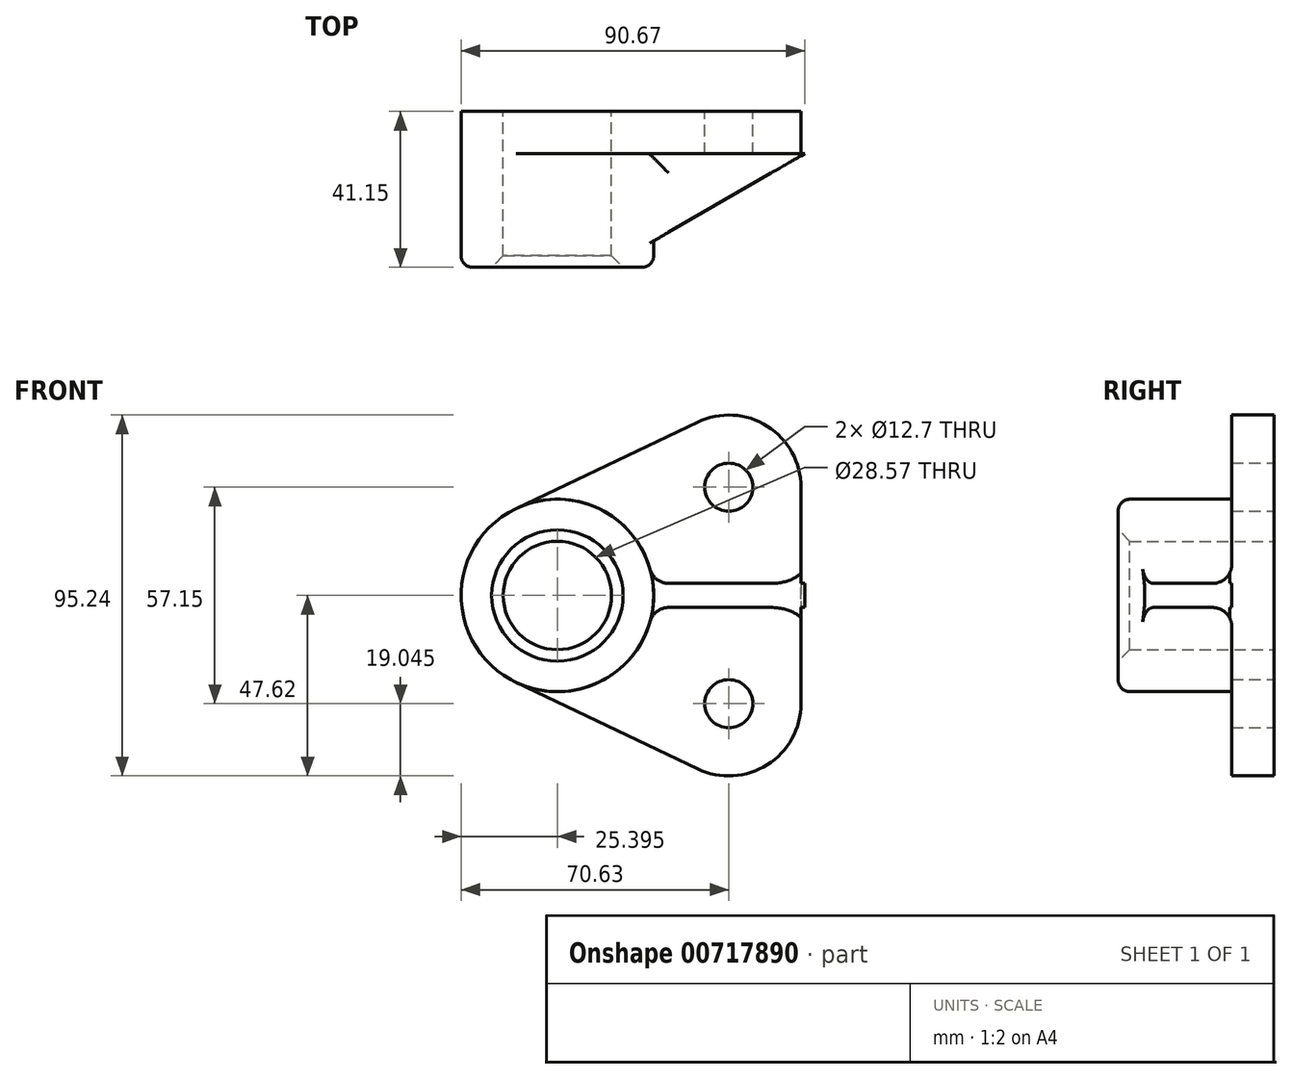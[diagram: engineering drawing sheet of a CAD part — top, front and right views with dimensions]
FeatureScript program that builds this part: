
annotation { "Feature Type Name" : "Feature", "Feature Type Description" : "" }
export const myFeature = defineFeature(function(context is Context, id is Id, definition is map)
    precondition{}
    {
        {
            var Q0;
            Q0=qCreatedBy(makeId("Front.planeOp"),FACE);
            var sketch = newSketch(context, id + "F0", { "sketchPlane" : qUnion([Q0])});
            skCircle(sketch, "E0", {"center": v(-45.23, 0) * mm, "radius": 25.4 * mm});
            skCircle(sketch, "E1", {"center": v(-45.23, 0) * mm, "radius": 14.29 * mm});
            skArc(sketch, "E2", {"start": v(19.05, 28.58) * mm, "mid": v(10.17, 44.68) * mm, "end": v(-8.2, 45.77) * mm});
            skLineSegment(sketch, "E3", {"start": v(-56.16, 22.93) * mm, "end": v(-8.2, 45.77) * mm});
            skLineSegment(sketch, "E4", {"start": v(19.05, 28.58) * mm, "end": v(19.05, -26.35) * mm});
            skLineSegment(sketch, "E5", {"start": v(-115.36, 0) * mm, "end": v(38.05, 0) * mm, "construction": true});
            skLineSegment(sketch, "E6.MirrorCS", {"start": v(-56.16, -22.93) * mm, "end": v(-8.2, -45.77) * mm});
            skArc(sketch, "E7.MirrorCS", {"start": v(19.05, -28.58) * mm, "mid": v(10.17, -44.68) * mm, "end": v(-8.2, -45.77) * mm});
            skLineSegment(sketch, "E8.MirrorCS", {"start": v(19.05, -28.58) * mm, "end": v(19.05, 26.35) * mm});
            skPoint(sketch, "E9.center.orphan", {"position": v(0, -26.35) * mm});
            skCircle(sketch, "E10", {"center": v(0, 28.58) * mm, "radius": 6.35 * mm});
            skCircle(sketch, "E11.MirrorC", {"center": v(0, -28.58) * mm, "radius": 6.35 * mm});
            skLineSegment(sketch, "E12", {"start": v(0, 28.58) * mm, "end": v(56.35, 28.58) * mm, "construction": true});
            skLineSegment(sketch, "E13", {"start": v(0, -28.58) * mm, "end": v(53.4, -28.58) * mm, "construction": true});
            skSolve(sketch);
        }
        {
            var Q0;
            Q0=makeQuery(id+"F0.imprint","IMPRINT",FACE,{"disambiguationData":[TD([[makeQuery(id+"F0.imprint","IMPRINT",EDGE,{"derivedFrom":sQuery(id+"F0.wireOp",EDGE,"E1")}),-1.0]])]});
            extrude(context, id + "F1", {"entities" : qUnion([Q0]), "depth" : 41.15 * mm, "offsetDistance" : 25.4 * mm});
        }
        {
            var Q0;
            Q0=makeQuery(id+"F1.opExtrude","CAP_EDGE",EDGE,{"disambiguationData":[OSD([sQuery(id+"F0.wireOp",EDGE,"E0")])],"isStart":false});
            fillet(context, id + "F2", {"entities" : qUnion([Q0]), "radius" : 3.05 * mm, "tangentPropagation" : true, "allowEdgeOverflow" : false});
        }
        {
            var Q0;
            Q0=makeQuery(id+"F1.opExtrude","CAP_EDGE",EDGE,{"disambiguationData":[OSD([sQuery(id+"F0.wireOp",EDGE,"E1")])],"isStart":false});
            chamfer(context, id + "F3", {"entities" : qUnion([Q0]), "width" : 3.05 * mm, "tangentPropagation" : true});
        }
        {
            var Q0;
            Q0=makeQuery(id+"F0.imprint","IMPRINT",FACE,{"disambiguationData":[TD([[makeQuery(id+"F0.imprint","IMPRINT",EDGE,{"derivedFrom":sQuery(id+"F0.wireOp",EDGE,"E2")}),1.0]])]});
            extrude(context, id + "F4", {"entities" : qUnion([Q0]), "operationType" : NewBodyOperationType.ADD, "depth" : 11.18 * mm, "offsetDistance" : 25.4 * mm});
        }
        {
            var Q0;
            Q0=qCreatedBy(makeId("Top.planeOp"),FACE);
            var sketch = newSketch(context, id + "F5", { "sketchPlane" : qUnion([Q0])});
            skLineSegment(sketch, "E14", {"start": v(-20.38, -11.14) * mm, "end": v(20.04, -11.14) * mm});
            skLineSegment(sketch, "E15", {"start": v(20.04, -11.14) * mm, "end": v(-20.38, -34.48) * mm});
            skLineSegment(sketch, "E16", {"start": v(-20.38, -34.48) * mm, "end": v(-20.38, -11.14) * mm});
            skSolve(sketch);
        }
        {
            var Q0;
            Q0=makeQuery(id+"F5.imprint","IMPRINT",FACE,{"disambiguationData":[TD([[makeQuery(id+"F5.imprint","IMPRINT",EDGE,{"derivedFrom":sQuery(id+"F5.wireOp",EDGE,"E14")}),-1.0]])]});
            var sketch = newSketch(context, id + "F6", { "sketchPlane" : qUnion([Q0])});
            skSolve(sketch);
        }
        {
            var Q0;
            Q0=makeQuery(id+"F6.imprint","IMPRINT",FACE,{"disambiguationData":[TD([[makeQuery(id+"F6.imprint","IMPRINT",EDGE,{"derivedFrom":makeQuery(id+"F5.imprint","IMPRINT",EDGE,{"derivedFrom":sQuery(id+"F5.wireOp",EDGE,"E14")})}),-1.0]])]});
            extrude(context, id + "F7", {"entities" : qUnion([Q0]), "operationType" : NewBodyOperationType.ADD, "endBound" : BoundingType.SYMMETRIC, "depth" : 6.35 * mm, "offsetDistance" : 25.4 * mm});
        }
        {
            var Q0;
            {var subQ0=sQuery(id+"F0.wireOp",EDGE,"E0");var subQ1=sQuery(id+"F0.wireOp",EDGE,"E6.MirrorCS");Q0=makeQuery(id+"F7.boolean.opBoolean","SPLIT",EDGE,{"disambiguationData":[TD([makeQuery(id+"F4.opExtrude","SWEPT_FACE",FACE,{"disambiguationData":[OSD([subQ1])]})])],"derivedFrom":makeQuery(id+"F4.opExtrude","CAP_EDGE",EDGE,{"disambiguationData":[OSD([subQ0])],"isStart":false})});}
            var Q1;
            Q1=makeQuery(id+"F7.boolean.opBoolean","INTERSECT",EDGE,{"derivedFrom":[makeQuery(id+"F4.opExtrude","CAP_FACE",FACE,{"disambiguationData":[OSD([sQuery(id+"F0.wireOp",EDGE,"E0"),sQuery(id+"F0.wireOp",EDGE,"E2"),sQuery(id+"F0.wireOp",EDGE,"E3"),sQuery(id+"F0.wireOp",EDGE,"E4"),sQuery(id+"F0.wireOp",EDGE,"E6.MirrorCS"),sQuery(id+"F0.wireOp",EDGE,"E7.MirrorCS"),sQuery(id+"F0.wireOp",EDGE,"E8.MirrorCS"),sQuery(id+"F0.wireOp",EDGE,"E10"),sQuery(id+"F0.wireOp",EDGE,"E11.MirrorC")])],"isStart":false}),makeQuery(id+"F7.opExtrude","CAP_FACE",FACE,{"disambiguationData":[OSD([sQuery(id+"F5.wireOp",EDGE,"E14"),sQuery(id+"F5.wireOp",EDGE,"E15"),sQuery(id+"F5.wireOp",EDGE,"E16")])],"isStart":true})]});
            var Q2;
            Q2=makeQuery(id+"F7.boolean.opBoolean","INTERSECT",EDGE,{"derivedFrom":[makeQuery(id+"F4.opExtrude","CAP_FACE",FACE,{"disambiguationData":[OSD([sQuery(id+"F0.wireOp",EDGE,"E0"),sQuery(id+"F0.wireOp",EDGE,"E2"),sQuery(id+"F0.wireOp",EDGE,"E3"),sQuery(id+"F0.wireOp",EDGE,"E4"),sQuery(id+"F0.wireOp",EDGE,"E6.MirrorCS"),sQuery(id+"F0.wireOp",EDGE,"E7.MirrorCS"),sQuery(id+"F0.wireOp",EDGE,"E8.MirrorCS"),sQuery(id+"F0.wireOp",EDGE,"E10"),sQuery(id+"F0.wireOp",EDGE,"E11.MirrorC")])],"isStart":false}),makeQuery(id+"F7.opExtrude","CAP_FACE",FACE,{"disambiguationData":[OSD([sQuery(id+"F5.wireOp",EDGE,"E14"),sQuery(id+"F5.wireOp",EDGE,"E15"),sQuery(id+"F5.wireOp",EDGE,"E16")])],"isStart":false})]});
            var Q3;
            {var subQ0=sQuery(id+"F0.wireOp",EDGE,"E0");var subQ1=sQuery(id+"F0.wireOp",EDGE,"E3");Q3=makeQuery(id+"F7.boolean.opBoolean","SPLIT",EDGE,{"disambiguationData":[TD([makeQuery(id+"F4.opExtrude","SWEPT_FACE",FACE,{"disambiguationData":[OSD([subQ1])]})])],"derivedFrom":makeQuery(id+"F4.opExtrude","CAP_EDGE",EDGE,{"disambiguationData":[OSD([subQ0])],"isStart":false})});}
            var Q4;
            Q4=makeQuery(id+"F7.boolean.opBoolean","INTERSECT",EDGE,{"derivedFrom":[makeQuery(id+"F1.opExtrude","SWEPT_FACE",FACE,{"disambiguationData":[OSD([sQuery(id+"F0.wireOp",EDGE,"E0")])]}),makeQuery(id+"F7.opExtrude","CAP_FACE",FACE,{"disambiguationData":[OSD([sQuery(id+"F5.wireOp",EDGE,"E14"),sQuery(id+"F5.wireOp",EDGE,"E15"),sQuery(id+"F5.wireOp",EDGE,"E16")])],"isStart":true})]});
            var Q5;
            Q5=makeQuery(id+"F7.boolean.opBoolean","INTERSECT",EDGE,{"derivedFrom":[makeQuery(id+"F1.opExtrude","SWEPT_FACE",FACE,{"disambiguationData":[OSD([sQuery(id+"F0.wireOp",EDGE,"E0")])]}),makeQuery(id+"F7.opExtrude","CAP_FACE",FACE,{"disambiguationData":[OSD([sQuery(id+"F5.wireOp",EDGE,"E14"),sQuery(id+"F5.wireOp",EDGE,"E15"),sQuery(id+"F5.wireOp",EDGE,"E16")])],"isStart":false})]});
            fillet(context, id + "F8", {"entities" : qUnion([Q0, Q1, Q2, Q3, Q4, Q5]), "radius" : 5.08 * mm, "tangentPropagation" : true, "allowEdgeOverflow" : false});
        }
    });
